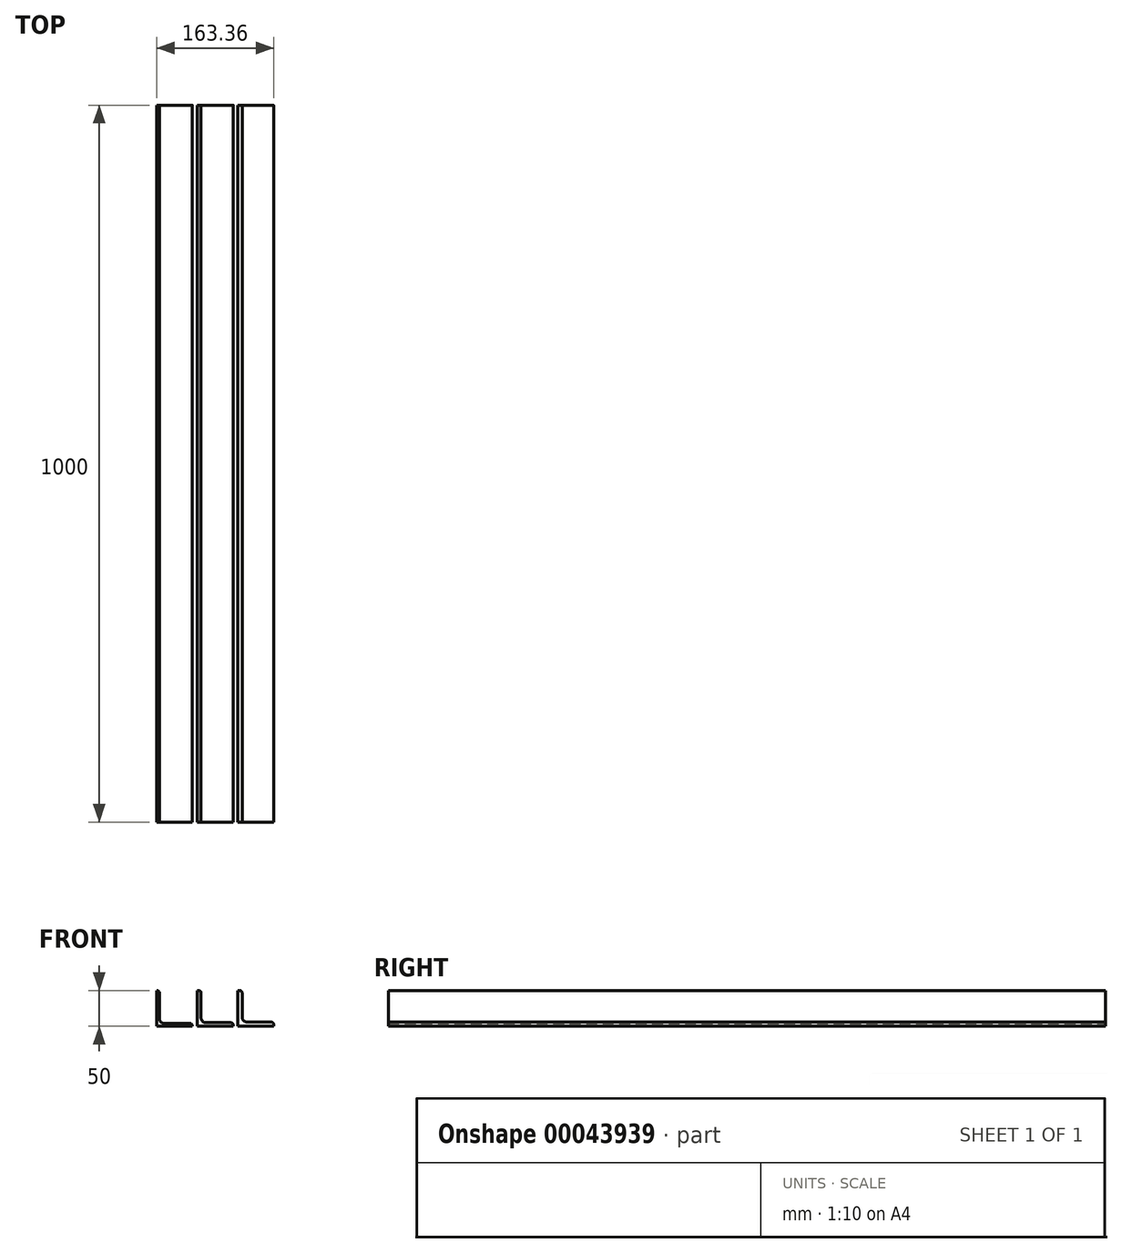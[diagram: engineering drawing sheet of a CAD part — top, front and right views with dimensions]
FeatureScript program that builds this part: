
annotation { "Feature Type Name" : "Feature", "Feature Type Description" : "" }
export const myFeature = defineFeature(function(context is Context, id is Id, definition is map)
    precondition{}
    {
        {
            var Q0;
            Q0=qCreatedBy(makeId("Front.planeOp"),FACE);
            var sketch = newSketch(context, id + "F0", { "sketchPlane" : qUnion([Q0])});
            skLineSegment(sketch, "E0", {"start": v(-89.05, 50) * mm, "end": v(-89.05, 0) * mm});
            skLineSegment(sketch, "E1", {"start": v(-89.05, 0) * mm, "end": v(-39.05, 0) * mm});
            skLineSegment(sketch, "E2", {"start": v(-39.05, 0) * mm, "end": v(-39.05, 4) * mm});
            skLineSegment(sketch, "E3", {"start": v(-39.05, 4) * mm, "end": v(-85.05, 4) * mm});
            skLineSegment(sketch, "E4", {"start": v(-85.05, 4) * mm, "end": v(-85.05, 50) * mm});
            skLineSegment(sketch, "E5", {"start": v(-85.05, 50) * mm, "end": v(-89.05, 50) * mm});
            skSolve(sketch);
        }
        {
            var Q0;
            Q0=makeQuery(id+"F0.imprint","IMPRINT",FACE,{"disambiguationData":[TD([[makeQuery(id+"F0.imprint","IMPRINT",EDGE,{"derivedFrom":sQuery(id+"F0.wireOp",EDGE,"E0")}),1.0]])]});
            extrude(context, id + "F1", {"entities" : qUnion([Q0]), "depth" : 1000 * mm});
        }
        {
            var Q0;
            Q0=makeQuery(id+"F1.opExtrude","SWEPT_EDGE",EDGE,{"disambiguationData":[OSD([sQuery(id+"F0.wireOp",EDGE,"E4"),sQuery(id+"F0.wireOp",EDGE,"E5")])]});
            var Q1;
            Q1=makeQuery(id+"F1.opExtrude","SWEPT_EDGE",EDGE,{"disambiguationData":[OSD([sQuery(id+"F0.wireOp",EDGE,"E2"),sQuery(id+"F0.wireOp",EDGE,"E3")])]});
            fillet(context, id + "F2", {"entities" : qUnion([Q0, Q1]), "radius" : 3.5 * mm, "tangentPropagation" : true, "allowEdgeOverflow" : false});
        }
        {
            var Q0;
            Q0=makeQuery(id+"F1.opExtrude","SWEPT_EDGE",EDGE,{"disambiguationData":[OSD([sQuery(id+"F0.wireOp",EDGE,"E3"),sQuery(id+"F0.wireOp",EDGE,"E4")])]});
            fillet(context, id + "F3", {"entities" : qUnion([Q0]), "radius" : 7 * mm, "tangentPropagation" : true, "allowEdgeOverflow" : false});
        }
        {
            var Q0;
            Q0=qCreatedBy(makeId("Front.planeOp"),FACE);
            var sketch = newSketch(context, id + "F4", { "sketchPlane" : qUnion([Q0])});
            skLineSegment(sketch, "E6", {"start": v(-32.01, 50) * mm, "end": v(-32.01, 0) * mm});
            skLineSegment(sketch, "E7", {"start": v(-32.01, 0) * mm, "end": v(17.99, 0) * mm});
            skLineSegment(sketch, "E8", {"start": v(17.99, 0) * mm, "end": v(17.99, 5) * mm});
            skLineSegment(sketch, "E9", {"start": v(17.99, 5) * mm, "end": v(-27.01, 5) * mm});
            skLineSegment(sketch, "E10", {"start": v(-27.01, 5) * mm, "end": v(-27.01, 50) * mm});
            skLineSegment(sketch, "E11", {"start": v(-27.01, 50) * mm, "end": v(-32.01, 50) * mm});
            skSolve(sketch);
        }
        {
            var Q0;
            Q0 = qSketchRegion(id + "F4", true);
            extrude(context, id + "F5", {"entities" : qUnion([Q0]), "depth" : 1000 * mm});
        }
        {
            var Q0;
            Q0=makeQuery(id+"F5.opExtrude","SWEPT_EDGE",EDGE,{"disambiguationData":[OSD([sQuery(id+"F4.wireOp",EDGE,"E8"),sQuery(id+"F4.wireOp",EDGE,"E9")])]});
            var Q1;
            Q1=makeQuery(id+"F5.opExtrude","SWEPT_EDGE",EDGE,{"disambiguationData":[OSD([sQuery(id+"F4.wireOp",EDGE,"E10"),sQuery(id+"F4.wireOp",EDGE,"E11")])]});
            fillet(context, id + "F6", {"entities" : qUnion([Q0, Q1]), "radius" : 3.5 * mm, "tangentPropagation" : true, "allowEdgeOverflow" : false});
        }
        {
            var Q0;
            Q0=makeQuery(id+"F5.opExtrude","SWEPT_EDGE",EDGE,{"disambiguationData":[OSD([sQuery(id+"F4.wireOp",EDGE,"E9"),sQuery(id+"F4.wireOp",EDGE,"E10")])]});
            fillet(context, id + "F7", {"entities" : qUnion([Q0]), "radius" : 7 * mm, "tangentPropagation" : true, "allowEdgeOverflow" : false});
        }
        {
            var Q0;
            Q0=qCreatedBy(makeId("Front.planeOp"),FACE);
            var sketch = newSketch(context, id + "F8", { "sketchPlane" : qUnion([Q0])});
            skLineSegment(sketch, "E12", {"start": v(24.31, 50) * mm, "end": v(24.31, 0) * mm});
            skLineSegment(sketch, "E13", {"start": v(24.31, 0) * mm, "end": v(74.31, 0) * mm});
            skLineSegment(sketch, "E14", {"start": v(74.31, 0) * mm, "end": v(74.31, 6) * mm});
            skLineSegment(sketch, "E15", {"start": v(74.31, 6) * mm, "end": v(30.31, 6) * mm});
            skLineSegment(sketch, "E16", {"start": v(30.31, 6) * mm, "end": v(30.31, 50) * mm});
            skLineSegment(sketch, "E17", {"start": v(30.31, 50) * mm, "end": v(24.31, 50) * mm});
            skSolve(sketch);
        }
        {
            var Q0;
            Q0 = qSketchRegion(id + "F8", true);
            extrude(context, id + "F9", {"entities" : qUnion([Q0]), "depth" : 1000 * mm});
        }
        {
            var Q0;
            Q0=makeQuery(id+"F9.opExtrude","SWEPT_EDGE",EDGE,{"disambiguationData":[OSD([sQuery(id+"F8.wireOp",EDGE,"E16"),sQuery(id+"F8.wireOp",EDGE,"E17")])]});
            var Q1;
            Q1=makeQuery(id+"F9.opExtrude","SWEPT_EDGE",EDGE,{"disambiguationData":[OSD([sQuery(id+"F8.wireOp",EDGE,"E14"),sQuery(id+"F8.wireOp",EDGE,"E15")])]});
            fillet(context, id + "F10", {"entities" : qUnion([Q0, Q1]), "radius" : 3.5 * mm, "tangentPropagation" : true, "allowEdgeOverflow" : false});
        }
        {
            var Q0;
            Q0=makeQuery(id+"F9.opExtrude","SWEPT_EDGE",EDGE,{"disambiguationData":[OSD([sQuery(id+"F8.wireOp",EDGE,"E15"),sQuery(id+"F8.wireOp",EDGE,"E16")])]});
            fillet(context, id + "F11", {"entities" : qUnion([Q0]), "radius" : 7 * mm, "tangentPropagation" : true, "allowEdgeOverflow" : false});
        }
    });
